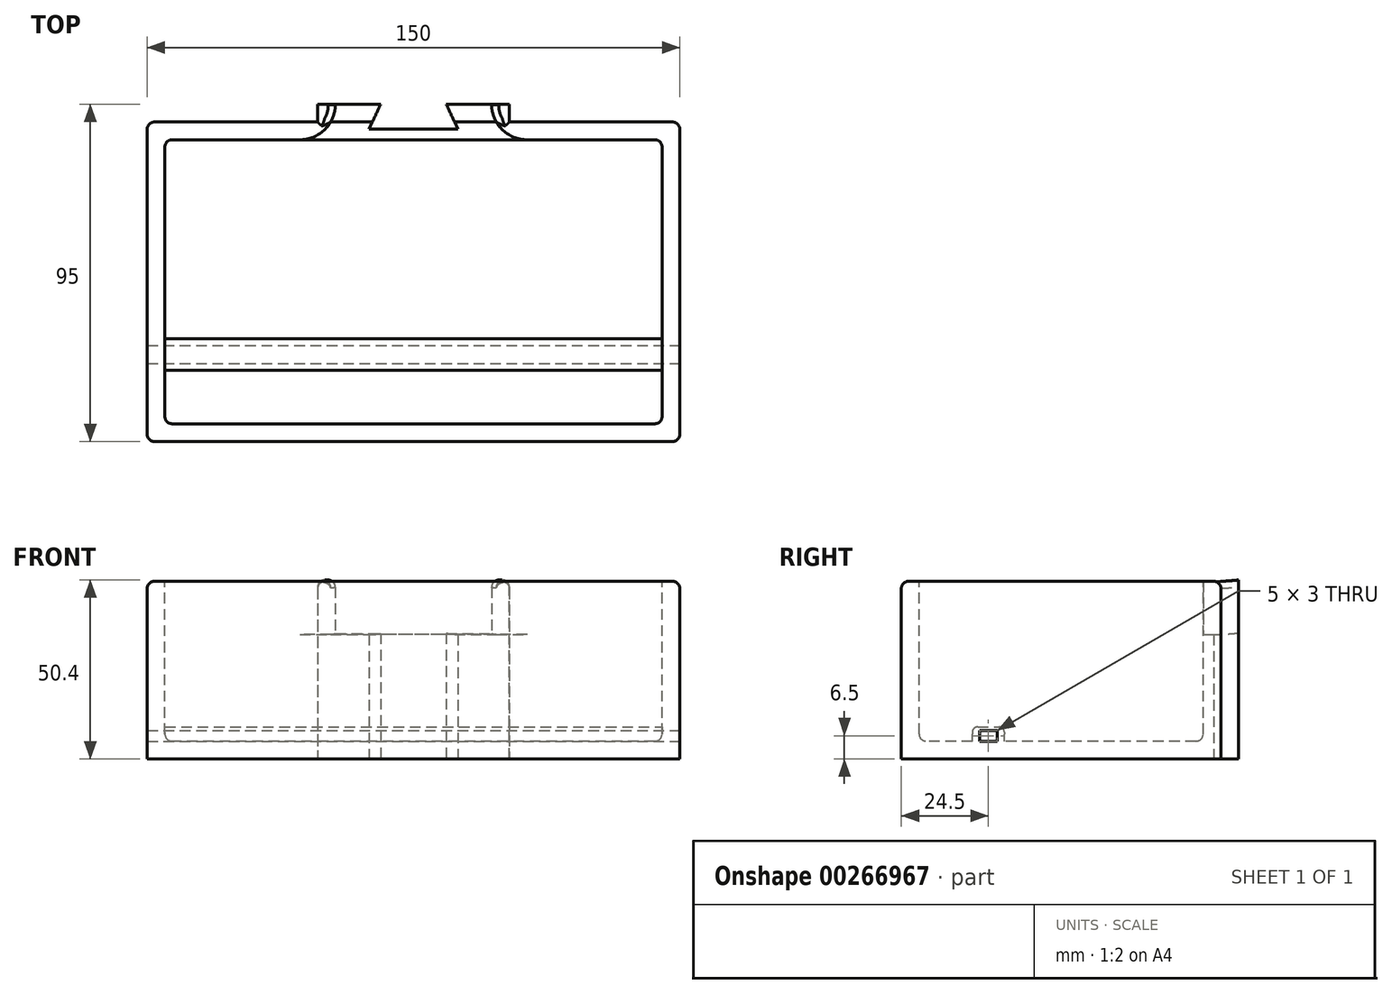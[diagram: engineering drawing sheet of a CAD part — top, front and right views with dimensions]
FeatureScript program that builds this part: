
annotation { "Feature Type Name" : "Feature", "Feature Type Description" : "" }
export const myFeature = defineFeature(function(context is Context, id is Id, definition is map)
    precondition{}
    {
        {
            var Q0;
            Q0=qCreatedBy(makeId("Right.planeOp"),FACE);
            var sketch = newSketch(context, id + "F0", { "sketchPlane" : qUnion([Q0])});
            skLineSegment(sketch, "E0.top", {"start": v(0, 120) * mm, "end": v(-45, 120) * mm});
            skLineSegment(sketch, "E0.left", {"start": v(0, 0) * mm, "end": v(0, 120) * mm});
            skLineSegment(sketch, "E1.top", {"start": v(0, 0) * mm, "end": v(-150, 0) * mm});
            skArc(sketch, "E2", {"start": v(-150, 50) * mm, "mid": v(-88.02, 70.78) * mm, "end": v(-45, 120) * mm});
            skLineSegment(sketch, "E3", {"start": v(-150, 50) * mm, "end": v(-150, 0) * mm});
            skSolve(sketch);
        }
        {
            var Q0;
            Q0=makeQuery(id+"F0.imprint","IMPRINT",FACE,{"disambiguationData":[TD([[makeQuery(id+"F0.imprint","IMPRINT",EDGE,{"derivedFrom":sQuery(id+"F0.wireOp",EDGE,"E0.bottom")}),-1.0]])]});
            var Q1;
            Q1=makeQuery(id+"F0.imprint","IMPRINT",FACE,{"disambiguationData":[TD([[makeQuery(id+"F0.imprint","IMPRINT",EDGE,{"derivedFrom":sQuery(id+"F0.wireOp",EDGE,"E0.top")}),1.0]])]});
            extrude(context, id + "F1", {"entities" : qUnion([Q0, Q1]), "depth" : 27 * mm});
        }
        {
            var Q0;
            Q0=makeQuery(id+"F1.opExtrude","SWEPT_BODY",BODY,{"disambiguationData":[OSD([sQuery(id+"F0.wireOp",EDGE,"E0.bottom"),sQuery(id+"F0.wireOp",EDGE,"E0.top"),sQuery(id+"F0.wireOp",EDGE,"E0.left"),sQuery(id+"F0.wireOp",EDGE,"E1.bottom"),sQuery(id+"F0.wireOp",EDGE,"E1.top"),sQuery(id+"F0.wireOp",EDGE,"E1.right"),sQuery(id+"F0.wireOp",EDGE,"E2")])]});
            var Q1;
            Q1=qCreatedBy(makeId("Right.planeOp"),FACE);
            mirror(context, id + "F2", {"operationType" : NewBodyOperationType.ADD, "entities" : qUnion([Q0]), "mirrorPlane" : qUnion([Q1])});
        }
        {
            var Q0;
            Q0=qCreatedBy(makeId("Right.planeOp"),FACE);
            var sketch = newSketch(context, id + "F3", { "sketchPlane" : qUnion([Q0])});
            skArc(sketch, "E4.0", {"start": v(-150, 34.98) * mm, "mid": v(-83.11, 56.1) * mm, "end": v(-34.86, 107) * mm});
            skLineSegment(sketch, "E5.0", {"start": v(-4.86, 107) * mm, "end": v(-34.86, 107) * mm});
            skLineSegment(sketch, "E6", {"start": v(-4.86, 107) * mm, "end": v(-4.86, 120) * mm});
            skLineSegment(sketch, "E7", {"start": v(-150, 34.98) * mm, "end": v(-150, 58.04) * mm});
            skArc(sketch, "E8.0", {"start": v(-150, 58.04) * mm, "mid": v(-93.92, 76.5) * mm, "end": v(-54, 120) * mm});
            skLineSegment(sketch, "E9", {"start": v(-54, 120) * mm, "end": v(-4.86, 120) * mm});
            skSolve(sketch);
        }
        {
            var Q0;
            Q0 = qSketchRegion(id + "F3", true);
            extrude(context, id + "F4", {"entities" : qUnion([Q0]), "operationType" : NewBodyOperationType.REMOVE, "oppositeDirection" : true, "depth" : 22 * mm});
        }
        {
            var Q0;
            Q0 = qSketchRegion(id + "F3", true);
            extrude(context, id + "F5", {"entities" : qUnion([Q0]), "operationType" : NewBodyOperationType.REMOVE, "depth" : 22 * mm});
        }
        {
            var Q0;
            Q0=qCreatedBy(makeId("Right.planeOp"),FACE);
            var sketch = newSketch(context, id + "F6", { "sketchPlane" : qUnion([Q0])});
            skLineSegment(sketch, "E10.bottom", {"start": v(-150, 0) * mm, "end": v(-240, 0) * mm});
            skLineSegment(sketch, "E10.top", {"start": v(-150, 50) * mm, "end": v(-240, 50) * mm});
            skLineSegment(sketch, "E10.left", {"start": v(-150, 0) * mm, "end": v(-150, 50) * mm});
            skLineSegment(sketch, "E10.right", {"start": v(-240, 0) * mm, "end": v(-240, 50) * mm});
            skSolve(sketch);
        }
        {
            var Q0;
            Q0=makeQuery(id+"F6.imprint","IMPRINT",FACE,{"disambiguationData":[TD([[makeQuery(id+"F6.imprint","IMPRINT",EDGE,{"derivedFrom":sQuery(id+"F6.wireOp",EDGE,"E10.bottom")}),-1.0]])]});
            extrude(context, id + "F7", {"entities" : qUnion([Q0]), "operationType" : NewBodyOperationType.ADD, "endBound" : BoundingType.SYMMETRIC, "oppositeDirection" : true, "depth" : 150 * mm});
        }
        {
            var Q0;
            Q0=makeQuery(id+"F7.opExtrude","SWEPT_FACE",FACE,{"disambiguationData":[OSD([sQuery(id+"F6.wireOp",EDGE,"E10.top")])]});
            var sketch = newSketch(context, id + "F8", { "sketchPlane" : qUnion([Q0])});
            skLineSegment(sketch, "E11.bottom", {"start": v(-70, -155) * mm, "end": v(70, -155) * mm});
            skLineSegment(sketch, "E11.top", {"start": v(-70, -235) * mm, "end": v(70, -235) * mm});
            skLineSegment(sketch, "E11.left", {"start": v(-70, -155) * mm, "end": v(-70, -235) * mm});
            skLineSegment(sketch, "E11.right", {"start": v(70, -155) * mm, "end": v(70, -235) * mm});
            skPoint(sketch, "E11.middle", {"position": v(0, -195) * mm});
            skSolve(sketch);
        }
        {
            var Q0;
            Q0=makeQuery(id+"F8.imprint","IMPRINT",FACE,{"disambiguationData":[TD([[makeQuery(id+"F8.imprint","IMPRINT",EDGE,{"derivedFrom":sQuery(id+"F8.wireOp",EDGE,"E11.bottom")}),-1.0]])]});
            extrude(context, id + "F9", {"entities" : qUnion([Q0]), "operationType" : NewBodyOperationType.REMOVE, "oppositeDirection" : true, "depth" : 45 * mm});
        }
        {
            var Q0;
            {var subQ5=sQuery(id+"F3.wireOp",EDGE,"E4.0");Q0=makeQuery(id+"F7.boolean.opBoolean","SPLIT",FACE,{"disambiguationData":[TD([makeQuery(id+"F4.boolean.opBoolean","COPY",FACE,{"derivedFrom":makeQuery(id+"F4.opExtrude","SWEPT_FACE",FACE,{"disambiguationData":[OSD([subQ5])]})})])],"derivedFrom":makeQuery(id+"F7.opExtrude","SWEPT_FACE",FACE,{"disambiguationData":[OSD([sQuery(id+"F6.wireOp",EDGE,"E10.left")])]})});}
            extrude(context, id + "F10", {"entities" : qUnion([Q0]), "operationType" : NewBodyOperationType.REMOVE, "oppositeDirection" : true, "depth" : 25 * mm});
        }
        {
            var Q0;
            Q0=makeQuery(id+"F7.opExtrude","CAP_EDGE",EDGE,{"disambiguationData":[OSD([sQuery(id+"F6.wireOp",EDGE,"E10.right")])],"isStart":true});
            var Q1;
            Q1=makeQuery(id+"F7.opExtrude","CAP_EDGE",EDGE,{"disambiguationData":[OSD([sQuery(id+"F6.wireOp",EDGE,"E10.left")])],"isStart":true});
            var Q2;
            Q2=makeQuery(id+"F7.opExtrude","CAP_EDGE",EDGE,{"disambiguationData":[OSD([sQuery(id+"F6.wireOp",EDGE,"E10.right")])],"isStart":false});
            var Q3;
            Q3=makeQuery(id+"F7.opExtrude","CAP_EDGE",EDGE,{"disambiguationData":[OSD([sQuery(id+"F6.wireOp",EDGE,"E10.left")])],"isStart":false});
            var Q4;
            Q4=makeQuery(id+"F1.opExtrude","CAP_EDGE",EDGE,{"disambiguationData":[OSD([sQuery(id+"F0.wireOp",EDGE,"E2")])],"isStart":false});
            var Q5;
            {var subQ2=sQuery(id+"F6.wireOp",EDGE,"E10.left");var subQ3=sQuery(id+"F6.wireOp",EDGE,"E10.top");Q5=makeQuery(id+"F7.boolean.opBoolean","SPLIT",EDGE,{"disambiguationData":[TD([makeQuery(id+"F7.opExtrude","CAP_FACE",FACE,{"disambiguationData":[OSD([sQuery(id+"F6.wireOp",EDGE,"E10.bottom"),subQ3,subQ2,sQuery(id+"F6.wireOp",EDGE,"E10.right")])],"isStart":true})])],"derivedFrom":makeQuery(id+"F7.opExtrude","SWEPT_EDGE",EDGE,{"disambiguationData":[OSD([subQ3,subQ2])]})});}
            var Q6;
            Q6=makeQuery(id+"F7.opExtrude","CAP_EDGE",EDGE,{"disambiguationData":[OSD([sQuery(id+"F6.wireOp",EDGE,"E10.top")])],"isStart":true});
            var Q7;
            Q7=makeQuery(id+"F7.opExtrude","SWEPT_EDGE",EDGE,{"disambiguationData":[OSD([sQuery(id+"F6.wireOp",EDGE,"E10.top"),sQuery(id+"F6.wireOp",EDGE,"E10.right")])]});
            var Q8;
            Q8=makeQuery(id+"F7.opExtrude","CAP_EDGE",EDGE,{"disambiguationData":[OSD([sQuery(id+"F6.wireOp",EDGE,"E10.top")])],"isStart":false});
            var Q9;
            {var subQ2=sQuery(id+"F6.wireOp",EDGE,"E10.left");var subQ3=sQuery(id+"F6.wireOp",EDGE,"E10.top");Q9=makeQuery(id+"F7.boolean.opBoolean","SPLIT",EDGE,{"disambiguationData":[TD([makeQuery(id+"F7.opExtrude","CAP_FACE",FACE,{"disambiguationData":[OSD([sQuery(id+"F6.wireOp",EDGE,"E10.bottom"),subQ3,subQ2,sQuery(id+"F6.wireOp",EDGE,"E10.right")])],"isStart":false})])],"derivedFrom":makeQuery(id+"F7.opExtrude","SWEPT_EDGE",EDGE,{"disambiguationData":[OSD([subQ3,subQ2])]})});}
            var Q10;
            Q10=makeQuery(id+"F2.opPattern","COPY",EDGE,{"derivedFrom":makeQuery(id+"F1.opExtrude","CAP_EDGE",EDGE,{"disambiguationData":[OSD([sQuery(id+"F0.wireOp",EDGE,"E2")])],"isStart":false}),"instanceName":"1"});
            var Q11;
            Q11=makeQuery(id+"F1.opExtrude","CAP_EDGE",EDGE,{"disambiguationData":[OSD([sQuery(id+"F0.wireOp",EDGE,"E0.top")])],"isStart":false});
            var Q12;
            Q12=makeQuery(id+"F2.opPattern","COPY",EDGE,{"derivedFrom":makeQuery(id+"F1.opExtrude","CAP_EDGE",EDGE,{"disambiguationData":[OSD([sQuery(id+"F0.wireOp",EDGE,"E0.top")])],"isStart":false}),"instanceName":"1"});
            var Q13;
            {var subQ0=makeQuery(id+"F1.opExtrude","SWEPT_EDGE",EDGE,{"disambiguationData":[OSD([sQuery(id+"F0.wireOp",EDGE,"E0.top"),sQuery(id+"F0.wireOp",EDGE,"E0.left")])]});Q13=makeQuery(id+"F2.boolean.opBoolean","MERGE",EDGE,{"derivedFrom":[subQ0,makeQuery(id+"F2.opPattern","COPY",EDGE,{"derivedFrom":subQ0,"instanceName":"1"})]});}
            var Q14;
            Q14=makeQuery(id+"F1.opExtrude","CAP_EDGE",EDGE,{"disambiguationData":[OSD([sQuery(id+"F0.wireOp",EDGE,"E0.left")])],"isStart":false});
            var Q15;
            Q15=makeQuery(id+"F2.opPattern","COPY",EDGE,{"derivedFrom":makeQuery(id+"F1.opExtrude","CAP_EDGE",EDGE,{"disambiguationData":[OSD([sQuery(id+"F0.wireOp",EDGE,"E0.left")])],"isStart":false}),"instanceName":"1"});
            fillet(context, id + "F11", {"entities" : qUnion([Q0, Q1, Q2, Q3, Q4, Q5, Q6, Q7, Q8, Q9, Q10, Q11, Q12, Q13, Q14, Q15]), "radius" : 2 * mm, "tangentPropagation" : true, "allowEdgeOverflow" : false});
        }
        {
            var Q0;
            {var subQ0=sQuery(id+"F3.wireOp",EDGE,"E5.0");var subQ1=sQuery(id+"F3.wireOp",EDGE,"E4.0");Q0=makeQuery(id+"F5.boolean.opBoolean","MERGE",EDGE,{"derivedFrom":[makeQuery(id+"F4.boolean.opBoolean","COPY",EDGE,{"derivedFrom":makeQuery(id+"F4.opExtrude","SWEPT_EDGE",EDGE,{"disambiguationData":[OSD([subQ1,subQ0])]})}),makeQuery(id+"F5.opExtrude","SWEPT_EDGE",EDGE,{"disambiguationData":[OSD([subQ1,subQ0])]})]});}
            var Q1;
            Q1=makeQuery(id+"F10.boolean.opBoolean","INTERSECT",EDGE,{"derivedFrom":[makeQuery(id+"F9.boolean.opBoolean","COPY",FACE,{"derivedFrom":makeQuery(id+"F9.opExtrude","SWEPT_FACE",FACE,{"disambiguationData":[OSD([sQuery(id+"F8.wireOp",EDGE,"E11.bottom")])]})}),makeQuery(id+"F10.opExtrude","SWEPT_FACE",FACE,{"disambiguationData":[OSD([sQuery(id+"F3.wireOp",EDGE,"E4.0"),sQuery(id+"F3.wireOp",EDGE,"E7")])]})]});
            fillet(context, id + "F12", {"entities" : qUnion([Q0, Q1]), "radius" : 10 * mm, "tangentPropagation" : true, "allowEdgeOverflow" : false});
        }
        {
            var Q0;
            Q0=makeQuery(id+"F9.boolean.opBoolean","COPY",EDGE,{"derivedFrom":makeQuery(id+"F9.opExtrude","SWEPT_EDGE",EDGE,{"disambiguationData":[OSD([sQuery(id+"F8.wireOp",EDGE,"E11.top"),sQuery(id+"F8.wireOp",EDGE,"E11.left")])]})});
            var Q1;
            Q1=makeQuery(id+"F9.boolean.opBoolean","COPY",EDGE,{"derivedFrom":makeQuery(id+"F9.opExtrude","SWEPT_EDGE",EDGE,{"disambiguationData":[OSD([sQuery(id+"F8.wireOp",EDGE,"E11.bottom"),sQuery(id+"F8.wireOp",EDGE,"E11.left")])]})});
            var Q2;
            Q2=makeQuery(id+"F9.boolean.opBoolean","COPY",EDGE,{"derivedFrom":makeQuery(id+"F9.opExtrude","SWEPT_EDGE",EDGE,{"disambiguationData":[OSD([sQuery(id+"F8.wireOp",EDGE,"E11.top"),sQuery(id+"F8.wireOp",EDGE,"E11.right")])]})});
            var Q3;
            Q3=makeQuery(id+"F9.boolean.opBoolean","COPY",EDGE,{"derivedFrom":makeQuery(id+"F9.opExtrude","SWEPT_EDGE",EDGE,{"disambiguationData":[OSD([sQuery(id+"F8.wireOp",EDGE,"E11.bottom"),sQuery(id+"F8.wireOp",EDGE,"E11.right")])]})});
            var Q4;
            Q4=makeQuery(id+"F9.boolean.opBoolean","COPY",FACE,{"derivedFrom":makeQuery(id+"F9.opExtrude","CAP_FACE",FACE,{"disambiguationData":[OSD([sQuery(id+"F8.wireOp",EDGE,"E11.bottom"),sQuery(id+"F8.wireOp",EDGE,"E11.top"),sQuery(id+"F8.wireOp",EDGE,"E11.left"),sQuery(id+"F8.wireOp",EDGE,"E11.right")])],"isStart":false})});
            var Q5;
            {var subQ0=sQuery(id+"F3.wireOp",EDGE,"E7");Q5=makeQuery(id+"F10.boolean.opBoolean","INTERSECT",EDGE,{"derivedFrom":[makeQuery(id+"F9.boolean.opBoolean","COPY",FACE,{"derivedFrom":makeQuery(id+"F9.opExtrude","SWEPT_FACE",FACE,{"disambiguationData":[OSD([sQuery(id+"F8.wireOp",EDGE,"E11.bottom")])]})}),makeQuery(id+"F10.opExtrude","SWEPT_FACE",FACE,{"disambiguationData":[OSD([subQ0]),TDD([makeQuery(id+"F4.boolean.opBoolean","COPY",EDGE,{"derivedFrom":makeQuery(id+"F4.opExtrude","CAP_EDGE",EDGE,{"disambiguationData":[OSD([subQ0])],"isStart":false})})])]})]});}
            var Q6;
            {var subQ0=sQuery(id+"F3.wireOp",EDGE,"E7");Q6=makeQuery(id+"F10.boolean.opBoolean","INTERSECT",EDGE,{"derivedFrom":[makeQuery(id+"F9.boolean.opBoolean","COPY",FACE,{"derivedFrom":makeQuery(id+"F9.opExtrude","SWEPT_FACE",FACE,{"disambiguationData":[OSD([sQuery(id+"F8.wireOp",EDGE,"E11.bottom")])]})}),makeQuery(id+"F10.opExtrude","SWEPT_FACE",FACE,{"disambiguationData":[OSD([subQ0]),TDD([makeQuery(id+"F5.boolean.opBoolean","COPY",EDGE,{"derivedFrom":makeQuery(id+"F5.opExtrude","CAP_EDGE",EDGE,{"disambiguationData":[OSD([subQ0])],"isStart":false})})])]})]});}
            var Q7;
            {var subQ0=sQuery(id+"F8.wireOp",EDGE,"E11.bottom");Q7=makeQuery(id+"F10.boolean.opBoolean","SPLIT",EDGE,{"disambiguationData":[TD([makeQuery(id+"F9.boolean.opBoolean","COPY",FACE,{"derivedFrom":makeQuery(id+"F9.opExtrude","SWEPT_FACE",FACE,{"disambiguationData":[OSD([sQuery(id+"F8.wireOp",EDGE,"E11.left")])]})})])],"derivedFrom":makeQuery(id+"F9.boolean.opBoolean","COPY",EDGE,{"derivedFrom":makeQuery(id+"F9.opExtrude","CAP_EDGE",EDGE,{"disambiguationData":[OSD([subQ0])],"isStart":true})})});}
            var Q8;
            {var subQ1=sQuery(id+"F8.wireOp",EDGE,"E11.bottom");Q8=makeQuery(id+"F10.boolean.opBoolean","SPLIT",EDGE,{"disambiguationData":[TD([makeQuery(id+"F9.boolean.opBoolean","COPY",FACE,{"derivedFrom":makeQuery(id+"F9.opExtrude","SWEPT_FACE",FACE,{"disambiguationData":[OSD([sQuery(id+"F8.wireOp",EDGE,"E11.right")])]})})])],"derivedFrom":makeQuery(id+"F9.boolean.opBoolean","COPY",EDGE,{"derivedFrom":makeQuery(id+"F9.opExtrude","CAP_EDGE",EDGE,{"disambiguationData":[OSD([subQ1])],"isStart":true})})});}
            var Q9;
            {var subQ0=makeQuery(id+"F1.opExtrude","SWEPT_FACE",FACE,{"disambiguationData":[OSD([sQuery(id+"F0.wireOp",EDGE,"E2")])]});Q9=makeQuery(id+"F4.boolean.opBoolean","INTERSECT",EDGE,{"derivedFrom":[makeQuery(id+"F2.boolean.opBoolean","MERGE",FACE,{"derivedFrom":[subQ0,makeQuery(id+"F2.opPattern","COPY",FACE,{"derivedFrom":subQ0,"instanceName":"1"})]}),makeQuery(id+"F4.opExtrude","CAP_FACE",FACE,{"disambiguationData":[OSD([sQuery(id+"F3.wireOp",EDGE,"E4.0"),sQuery(id+"F3.wireOp",EDGE,"E5.0"),sQuery(id+"F3.wireOp",EDGE,"E6"),sQuery(id+"F3.wireOp",EDGE,"E7"),sQuery(id+"F3.wireOp",EDGE,"E8.0"),sQuery(id+"F3.wireOp",EDGE,"E9")])],"isStart":false})]});}
            var Q10;
            {var subQ0=sQuery(id+"F3.wireOp",EDGE,"E9");var subQ1=sQuery(id+"F3.wireOp",EDGE,"E8.0");var subQ2=sQuery(id+"F3.wireOp",EDGE,"E7");var subQ3=sQuery(id+"F3.wireOp",EDGE,"E6");var subQ4=sQuery(id+"F3.wireOp",EDGE,"E5.0");var subQ5=sQuery(id+"F3.wireOp",EDGE,"E4.0");var subQ6=sQuery(id+"F0.wireOp",EDGE,"E0.top");var subQ8=sQuery(id+"F0.wireOp",EDGE,"E3");var subQ10=sQuery(id+"F0.wireOp",EDGE,"E2");var subQ11=makeQuery(id+"F1.opExtrude","SWEPT_FACE",FACE,{"disambiguationData":[OSD([subQ10])]});Q10=makeQuery(id+"F5.boolean.opBoolean","INTERSECT",EDGE,{"derivedFrom":[makeQuery(id+"F4.boolean.opBoolean","SPLIT",FACE,{"disambiguationData":[TD([makeQuery(id+"F1.opExtrude","CAP_FACE",FACE,{"disambiguationData":[OSD([subQ6,sQuery(id+"F0.wireOp",EDGE,"E0.left"),sQuery(id+"F0.wireOp",EDGE,"E1.top"),subQ10,subQ8])],"isStart":false})])],"derivedFrom":makeQuery(id+"F2.boolean.opBoolean","MERGE",FACE,{"derivedFrom":[subQ11,makeQuery(id+"F2.opPattern","COPY",FACE,{"derivedFrom":subQ11,"instanceName":"1"})]})}),makeQuery(id+"F5.opExtrude","CAP_FACE",FACE,{"disambiguationData":[OSD([subQ5,subQ4,subQ3,subQ2,subQ1,subQ0])],"isStart":false})]});}
            var Q11;
            Q11=makeQuery(id+"F4.boolean.opBoolean","COPY",EDGE,{"derivedFrom":makeQuery(id+"F4.opExtrude","CAP_EDGE",EDGE,{"disambiguationData":[OSD([sQuery(id+"F3.wireOp",EDGE,"E9")])],"isStart":false})});
            var Q12;
            Q12=makeQuery(id+"F5.boolean.opBoolean","COPY",EDGE,{"derivedFrom":makeQuery(id+"F5.opExtrude","CAP_EDGE",EDGE,{"disambiguationData":[OSD([sQuery(id+"F3.wireOp",EDGE,"E9")])],"isStart":false})});
            var Q13;
            {var subQ0=sQuery(id+"F3.wireOp",EDGE,"E9");var subQ1=sQuery(id+"F3.wireOp",EDGE,"E6");Q13=makeQuery(id+"F5.boolean.opBoolean","MERGE",EDGE,{"derivedFrom":[makeQuery(id+"F4.boolean.opBoolean","COPY",EDGE,{"derivedFrom":makeQuery(id+"F4.opExtrude","SWEPT_EDGE",EDGE,{"disambiguationData":[OSD([subQ1,subQ0])]})}),makeQuery(id+"F5.opExtrude","SWEPT_EDGE",EDGE,{"disambiguationData":[OSD([subQ1,subQ0])]})]});}
            fillet(context, id + "F13", {"entities" : qUnion([Q0, Q1, Q2, Q3, Q4, Q5, Q6, Q7, Q8, Q9, Q10, Q11, Q12, Q13]), "radius" : 2 * mm, "tangentPropagation" : true, "allowEdgeOverflow" : false});
        }
        {
            var Q0;
            Q0=qCreatedBy(makeId("Top.planeOp"),FACE);
            var sketch = newSketch(context, id + "F14", { "sketchPlane" : qUnion([Q0])});
            skLineSegment(sketch, "E12", {"start": v(-51.84, -145) * mm, "end": v(-9.24, -145) * mm});
            skLineSegment(sketch, "E13", {"start": v(0, -162.57) * mm, "end": v(0, 0) * mm, "construction": true});
            skLineSegment(sketch, "E14", {"start": v(-9.24, -145) * mm, "end": v(-12.5, -152) * mm});
            skLineSegment(sketch, "E15", {"start": v(-12.5, -152) * mm, "end": v(0, -152) * mm});
            skLineSegment(sketch, "E16", {"start": v(0, -152) * mm, "end": v(0, -145) * mm});
            skLineSegment(sketch, "E17.MirrorCS", {"start": v(9.24, -145) * mm, "end": v(12.5, -152) * mm});
            skLineSegment(sketch, "E18.MirrorCS", {"start": v(12.5, -152) * mm, "end": v(0, -152) * mm});
            skLineSegment(sketch, "E19.trimOffspring", {"start": v(9.24, -145) * mm, "end": v(70.03, -145) * mm});
            skLineSegment(sketch, "E20", {"start": v(-51.84, -145) * mm, "end": v(-51.84, 27.54) * mm});
            skLineSegment(sketch, "E21", {"start": v(-51.84, 27.54) * mm, "end": v(72.57, 27.54) * mm});
            skLineSegment(sketch, "E22", {"start": v(72.57, 27.54) * mm, "end": v(70.03, -145) * mm});
            skSolve(sketch);
        }
        {
            var Q0;
            Q0 = qSketchRegion(id + "F14", true);
            extrude(context, id + "F15", {"entities" : qUnion([Q0]), "operationType" : NewBodyOperationType.REMOVE, "depth" : 150 * mm});
        }
        {
            var Q0;
            Q0=makeQuery(id+"F7.opExtrude","CAP_FACE",FACE,{"disambiguationData":[OSD([sQuery(id+"F6.wireOp",EDGE,"E10.bottom"),sQuery(id+"F6.wireOp",EDGE,"E10.top"),sQuery(id+"F6.wireOp",EDGE,"E10.left"),sQuery(id+"F6.wireOp",EDGE,"E10.right")])],"isStart":true});
            var sketch = newSketch(context, id + "F16", { "sketchPlane" : qUnion([Q0])});
            skLineSegment(sketch, "E23.bottom", {"start": v(-211, 4) * mm, "end": v(-220, 4) * mm});
            skLineSegment(sketch, "E23.top", {"start": v(-211, 9) * mm, "end": v(-220, 9) * mm});
            skLineSegment(sketch, "E23.left", {"start": v(-211, 4) * mm, "end": v(-211, 9) * mm});
            skLineSegment(sketch, "E23.right", {"start": v(-220, 4) * mm, "end": v(-220, 9) * mm});
            skPoint(sketch, "E23.middle", {"position": v(-215.5, 6.5) * mm});
            skSolve(sketch);
        }
        {
            var Q0;
            Q0=makeQuery(id+"F16.imprint","IMPRINT",FACE,{"disambiguationData":[TD([[makeQuery(id+"F16.imprint","IMPRINT",EDGE,{"derivedFrom":sQuery(id+"F16.wireOp",EDGE,"FLO9fnOe-0lVf-23Zt-2ls3-FvlZIA6uB7u2.bottom")}),1.0]])]});
            var Q1;
            Q1=makeQuery(id+"F16.imprint","IMPRINT",FACE,{"disambiguationData":[TD([[makeQuery(id+"F16.imprint","IMPRINT",EDGE,{"derivedFrom":sQuery(id+"F16.wireOp",EDGE,"E23.bottom")}),-1.0]])]});
            extrude(context, id + "F17", {"entities" : qUnion([Q0, Q1]), "operationType" : NewBodyOperationType.ADD, "oppositeDirection" : true, "depth" : 149 * mm});
        }
        {
            var Q0;
            Q0=makeQuery(id+"F7.opExtrude","CAP_FACE",FACE,{"disambiguationData":[OSD([sQuery(id+"F6.wireOp",EDGE,"E10.bottom"),sQuery(id+"F6.wireOp",EDGE,"E10.top"),sQuery(id+"F6.wireOp",EDGE,"E10.left"),sQuery(id+"F6.wireOp",EDGE,"E10.right")])],"isStart":true});
            var sketch = newSketch(context, id + "F18", { "sketchPlane" : qUnion([Q0])});
            skLineSegment(sketch, "E24.bottom", {"start": v(-218, 8) * mm, "end": v(-213, 8) * mm});
            skLineSegment(sketch, "E24.top", {"start": v(-218, 5) * mm, "end": v(-213, 5) * mm});
            skLineSegment(sketch, "E24.left", {"start": v(-218, 8) * mm, "end": v(-218, 5) * mm});
            skLineSegment(sketch, "E24.right", {"start": v(-213, 8) * mm, "end": v(-213, 5) * mm});
            skSolve(sketch);
        }
        {
            var Q0;
            Q0=makeQuery(id+"F18.imprint","IMPRINT",FACE,{"disambiguationData":[TD([[makeQuery(id+"F18.imprint","IMPRINT",EDGE,{"derivedFrom":sQuery(id+"F18.wireOp",EDGE,"E24.bottom")}),-1.0]])]});
            extrude(context, id + "F19", {"entities" : qUnion([Q0]), "operationType" : NewBodyOperationType.REMOVE, "oppositeDirection" : true, "depth" : 160 * mm});
        }
        {
            var Q0;
            Q0=makeQuery(id+"F17.opExtrude","SWEPT_EDGE",EDGE,{"disambiguationData":[OSD([sQuery(id+"F16.wireOp",EDGE,"E23.top"),sQuery(id+"F16.wireOp",EDGE,"E23.left")])]});
            var Q1;
            Q1=makeQuery(id+"F17.opExtrude","SWEPT_EDGE",EDGE,{"disambiguationData":[OSD([sQuery(id+"F16.wireOp",EDGE,"E23.top"),sQuery(id+"F16.wireOp",EDGE,"E23.right")])]});
            fillet(context, id + "F20", {"entities" : qUnion([Q0, Q1]), "radius" : 1.5 * mm, "tangentPropagation" : true, "allowEdgeOverflow" : false});
        }
    });
